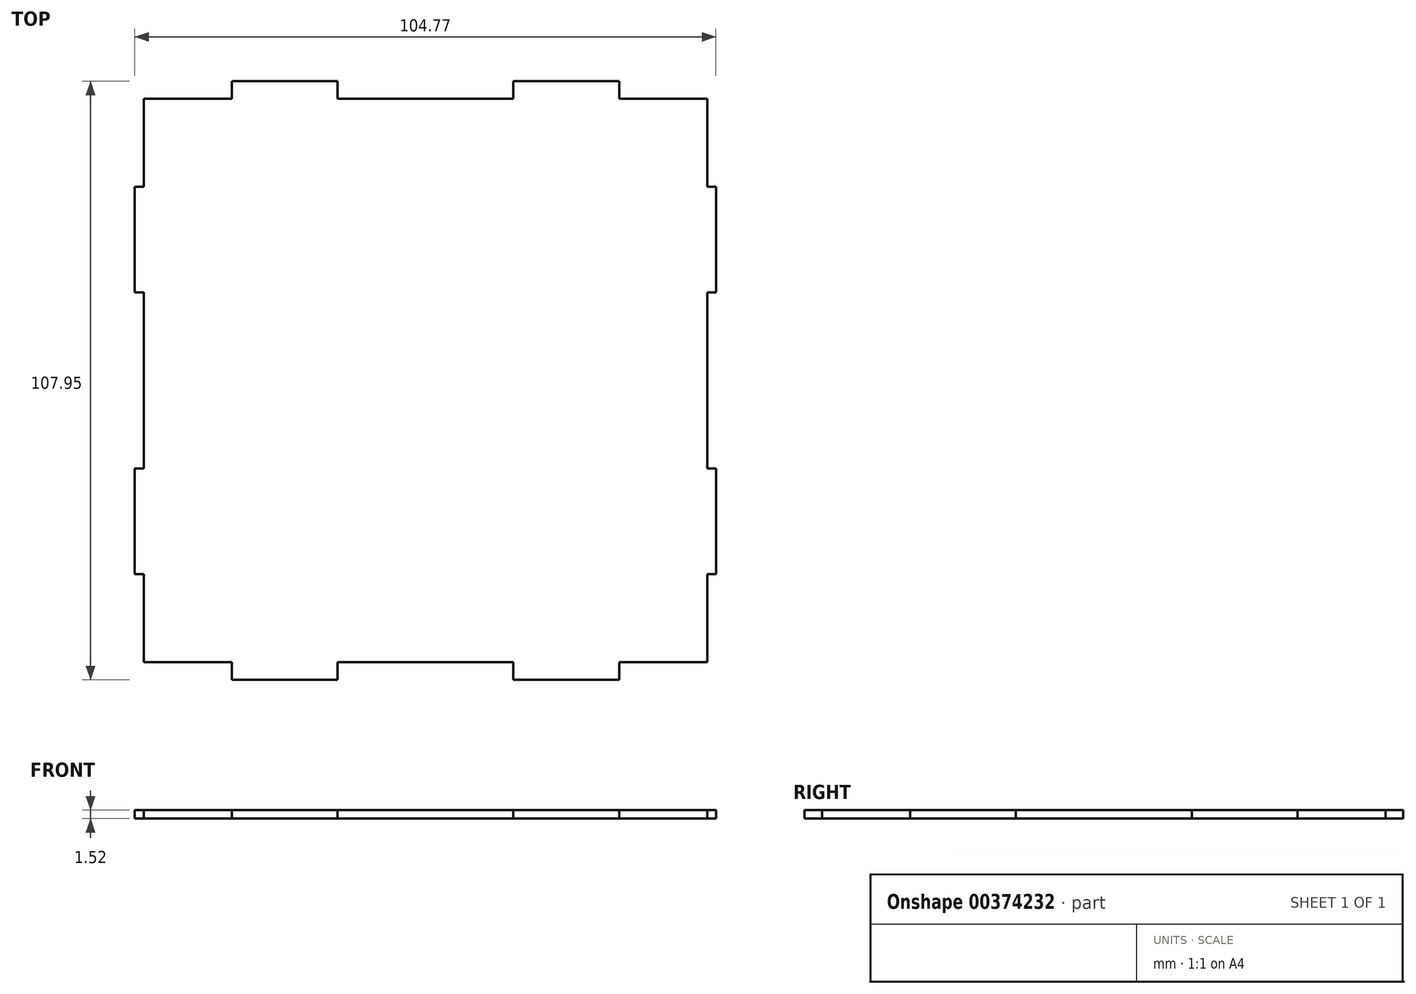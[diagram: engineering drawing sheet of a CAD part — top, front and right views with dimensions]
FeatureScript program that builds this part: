
annotation { "Feature Type Name" : "Feature", "Feature Type Description" : "" }
export const myFeature = defineFeature(function(context is Context, id is Id, definition is map)
    precondition{}
    {
        {
            var Q0;
            Q0=qCreatedBy(makeId("Top.planeOp"),FACE);
            var sketch = newSketch(context, id + "F0", { "sketchPlane" : qUnion([Q0])});
            skLineSegment(sketch, "E0", {"start": v(-129.72, -42.86) * mm, "end": v(-128.13, -42.86) * mm});
            skLineSegment(sketch, "E1", {"start": v(-128.13, -42.86) * mm, "end": v(-128.13, -58.74) * mm});
            skLineSegment(sketch, "E2", {"start": v(-128.13, -58.74) * mm, "end": v(-112.26, -58.74) * mm});
            skLineSegment(sketch, "E3", {"start": v(-112.26, -58.74) * mm, "end": v(-112.26, -61.91) * mm});
            skLineSegment(sketch, "E4", {"start": v(-112.26, -61.91) * mm, "end": v(-93.2, -61.91) * mm});
            skLineSegment(sketch, "E5", {"start": v(-93.2, -61.91) * mm, "end": v(-93.2, -58.74) * mm});
            skLineSegment(sketch, "E6", {"start": v(-93.2, -58.74) * mm, "end": v(-61.46, -58.74) * mm});
            skLineSegment(sketch, "E7", {"start": v(-61.46, -58.74) * mm, "end": v(-61.46, -61.91) * mm});
            skLineSegment(sketch, "E8", {"start": v(-61.46, -61.91) * mm, "end": v(-42.4, -61.91) * mm});
            skLineSegment(sketch, "E9", {"start": v(-42.4, -61.91) * mm, "end": v(-42.4, -58.74) * mm});
            skLineSegment(sketch, "E10", {"start": v(-42.4, -58.74) * mm, "end": v(-26.53, -58.74) * mm});
            skLineSegment(sketch, "E11", {"start": v(-26.53, -58.74) * mm, "end": v(-26.53, -42.86) * mm});
            skLineSegment(sketch, "E12", {"start": v(-26.53, -42.86) * mm, "end": v(-24.95, -42.86) * mm});
            skLineSegment(sketch, "E13", {"start": v(-24.95, -42.86) * mm, "end": v(-24.95, -23.81) * mm});
            skLineSegment(sketch, "E14", {"start": v(-24.95, -23.81) * mm, "end": v(-26.53, -23.81) * mm});
            skLineSegment(sketch, "E15", {"start": v(-26.53, -23.81) * mm, "end": v(-26.53, 7.94) * mm});
            skLineSegment(sketch, "E16", {"start": v(-26.53, 7.94) * mm, "end": v(-24.95, 7.94) * mm});
            skLineSegment(sketch, "E17", {"start": v(-24.95, 7.94) * mm, "end": v(-24.95, 26.99) * mm});
            skLineSegment(sketch, "E18", {"start": v(-24.95, 26.99) * mm, "end": v(-26.53, 26.99) * mm});
            skLineSegment(sketch, "E19", {"start": v(-26.53, 26.99) * mm, "end": v(-26.53, 42.86) * mm});
            skLineSegment(sketch, "E20", {"start": v(-26.53, 42.86) * mm, "end": v(-42.4, 42.86) * mm});
            skLineSegment(sketch, "E21", {"start": v(-42.4, 42.86) * mm, "end": v(-42.4, 46.04) * mm});
            skLineSegment(sketch, "E22", {"start": v(-42.4, 46.04) * mm, "end": v(-61.46, 46.04) * mm});
            skLineSegment(sketch, "E23", {"start": v(-61.46, 46.04) * mm, "end": v(-61.46, 42.86) * mm});
            skLineSegment(sketch, "E24", {"start": v(-61.46, 42.86) * mm, "end": v(-93.2, 42.86) * mm});
            skLineSegment(sketch, "E25", {"start": v(-93.2, 42.86) * mm, "end": v(-93.2, 46.04) * mm});
            skLineSegment(sketch, "E26", {"start": v(-93.2, 46.04) * mm, "end": v(-112.26, 46.04) * mm});
            skLineSegment(sketch, "E27", {"start": v(-112.26, 46.04) * mm, "end": v(-112.26, 42.86) * mm});
            skLineSegment(sketch, "E28", {"start": v(-112.26, 42.86) * mm, "end": v(-128.13, 42.86) * mm});
            skLineSegment(sketch, "E29", {"start": v(-128.13, 42.86) * mm, "end": v(-128.13, 26.99) * mm});
            skLineSegment(sketch, "E30", {"start": v(-128.13, 26.99) * mm, "end": v(-129.72, 26.99) * mm});
            skLineSegment(sketch, "E31", {"start": v(-129.72, 26.99) * mm, "end": v(-129.72, 7.94) * mm});
            skLineSegment(sketch, "E32", {"start": v(-129.72, 7.94) * mm, "end": v(-128.13, 7.94) * mm});
            skLineSegment(sketch, "E33", {"start": v(-128.13, 7.94) * mm, "end": v(-128.13, -23.81) * mm});
            skLineSegment(sketch, "E34", {"start": v(-128.13, -23.81) * mm, "end": v(-129.72, -23.81) * mm});
            skLineSegment(sketch, "E35", {"start": v(-129.72, -23.81) * mm, "end": v(-129.72, -42.86) * mm});
            skSolve(sketch);
        }
        {
            var Q0;
            Q0=makeQuery(id+"F0.imprint","IMPRINT",FACE,{"disambiguationData":[TD([[makeQuery(id+"F0.imprint","IMPRINT",EDGE,{"derivedFrom":sQuery(id+"F0.wireOp",EDGE,"E0")}),1.0]])]});
            extrude(context, id + "F1", {"entities" : qUnion([Q0]), "depth" : 1.52 * mm});
        }
    });
